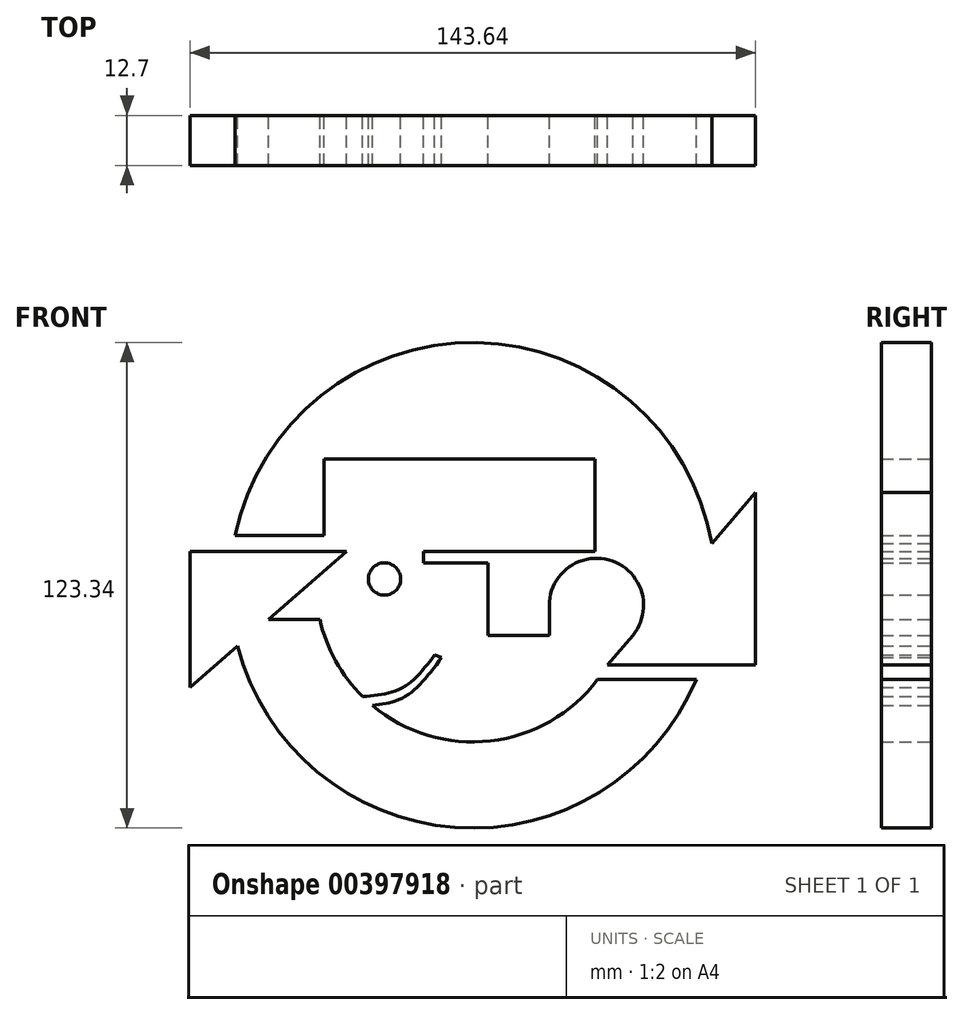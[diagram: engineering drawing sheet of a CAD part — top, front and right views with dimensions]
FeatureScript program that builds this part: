
annotation { "Feature Type Name" : "Feature", "Feature Type Description" : "" }
export const myFeature = defineFeature(function(context is Context, id is Id, definition is map)
    precondition{}
    {
        {
            var Q0;
            Q0=qCreatedBy(makeId("Front.planeOp"),FACE);
            var sketch = newSketch(context, id + "F0", { "sketchPlane" : qUnion([Q0])});
            skArc(sketch, "E0", {"start": v(60.75, 10.62) * mm, "mid": v(1.02, 61.66) * mm, "end": v(-60.37, 12.62) * mm});
            skArc(sketch, "E1", {"start": v(-38.81, -8.67) * mm, "mid": v(-34.8, -19.26) * mm, "end": v(-27.95, -28.3) * mm});
            skLineSegment(sketch, "E2", {"start": v(-60.37, 12.62) * mm, "end": v(-37.71, 12.62) * mm});
            skLineSegment(sketch, "E3", {"start": v(-37.71, 12.62) * mm, "end": v(-37.71, 32.1) * mm});
            skLineSegment(sketch, "E4", {"start": v(-37.71, 32.1) * mm, "end": v(31.1, 32.1) * mm});
            skLineSegment(sketch, "E5", {"start": v(31.1, 32.1) * mm, "end": v(31.1, 8.6) * mm});
            skLineSegment(sketch, "E6", {"start": v(31.1, 8.6) * mm, "end": v(-12.51, 8.6) * mm});
            skLineSegment(sketch, "E7", {"start": v(-12.51, 8.6) * mm, "end": v(-12.51, 5.7) * mm});
            skLineSegment(sketch, "E8", {"start": v(-12.51, 5.7) * mm, "end": v(3.9, 5.7) * mm});
            skLineSegment(sketch, "E9", {"start": v(3.9, 5.7) * mm, "end": v(3.9, -12.8) * mm});
            skLineSegment(sketch, "E10", {"start": v(3.9, -12.8) * mm, "end": v(19.47, -12.8) * mm});
            skLineSegment(sketch, "E11", {"start": v(19.47, -12.8) * mm, "end": v(19.47, -5.1) * mm});
            skLineSegment(sketch, "E12", {"start": v(71.84, 23.52) * mm, "end": v(71.84, -20.24) * mm});
            skLineSegment(sketch, "E13", {"start": v(71.84, 23.52) * mm, "end": v(60.75, 10.62) * mm});
            skLineSegment(sketch, "E14", {"start": v(34.23, -20.24) * mm, "end": v(71.84, -20.24) * mm});
            skArc(sketch, "E15", {"start": v(19.47, -5.1) * mm, "mid": v(35.49, 6.17) * mm, "end": v(40.7, -12.71) * mm});
            skLineSegment(sketch, "E16.trimOffspring", {"start": v(40.7, -12.71) * mm, "end": v(34.23, -20.24) * mm});
            skLineSegment(sketch, "E17", {"start": v(31.73, -23.97) * mm, "end": v(56.82, -23.97) * mm});
            skLineSegment(sketch, "E18", {"start": v(-31.98, 8.6) * mm, "end": v(-71.8, 8.6) * mm});
            skLineSegment(sketch, "E19", {"start": v(-71.8, 8.6) * mm, "end": v(-71.8, -25.93) * mm});
            skLineSegment(sketch, "E20", {"start": v(-71.8, -25.93) * mm, "end": v(-59.7, -15.44) * mm});
            skLineSegment(sketch, "E21", {"start": v(-51.9, -8.67) * mm, "end": v(-38.81, -8.67) * mm});
            skArc(sketch, "E22.trimOffspring", {"start": v(-59.7, -15.44) * mm, "mid": v(-4.5, -61.5) * mm, "end": v(56.82, -23.97) * mm});
            skLineSegment(sketch, "E23.trimOffspring", {"start": v(-51.9, -8.67) * mm, "end": v(-31.98, 8.6) * mm});
            skCircle(sketch, "E24", {"center": v(-22.4, 1.6) * mm, "radius": 4.09 * mm});
            skFitSpline(sketch, "E25", {"points": [v(-27.95, -28.3) * mm, v(-17.75, -26) * mm, v(-9.63, -17.65) * mm], "startDerivative": vector(22.16, 1.88) * mm, "endDerivative": vector(14.48, 19.2) * mm});
            skFitSpline(sketch, "E26", {"points": [v(-25.48, -30.53) * mm, v(-16.82, -28.08) * mm, v(-7.9, -18.35) * mm], "startDerivative": vector(19.75, 2.57) * mm, "endDerivative": vector(15.51, 21.13) * mm});
            skLineSegment(sketch, "E27", {"start": v(-9.63, -17.65) * mm, "end": v(-7.9, -18.35) * mm});
            skArc(sketch, "E28.trimOffspring", {"start": v(-25.48, -30.53) * mm, "mid": v(4.53, -39.5) * mm, "end": v(31.73, -23.97) * mm});
            skSolve(sketch);
        }
        {
            var Q0;
            Q0 = qSketchRegion(id + "F0", true);
            extrude(context, id + "F1", {"entities" : qUnion([Q0]), "depth" : 12.7 * mm});
        }
    });
